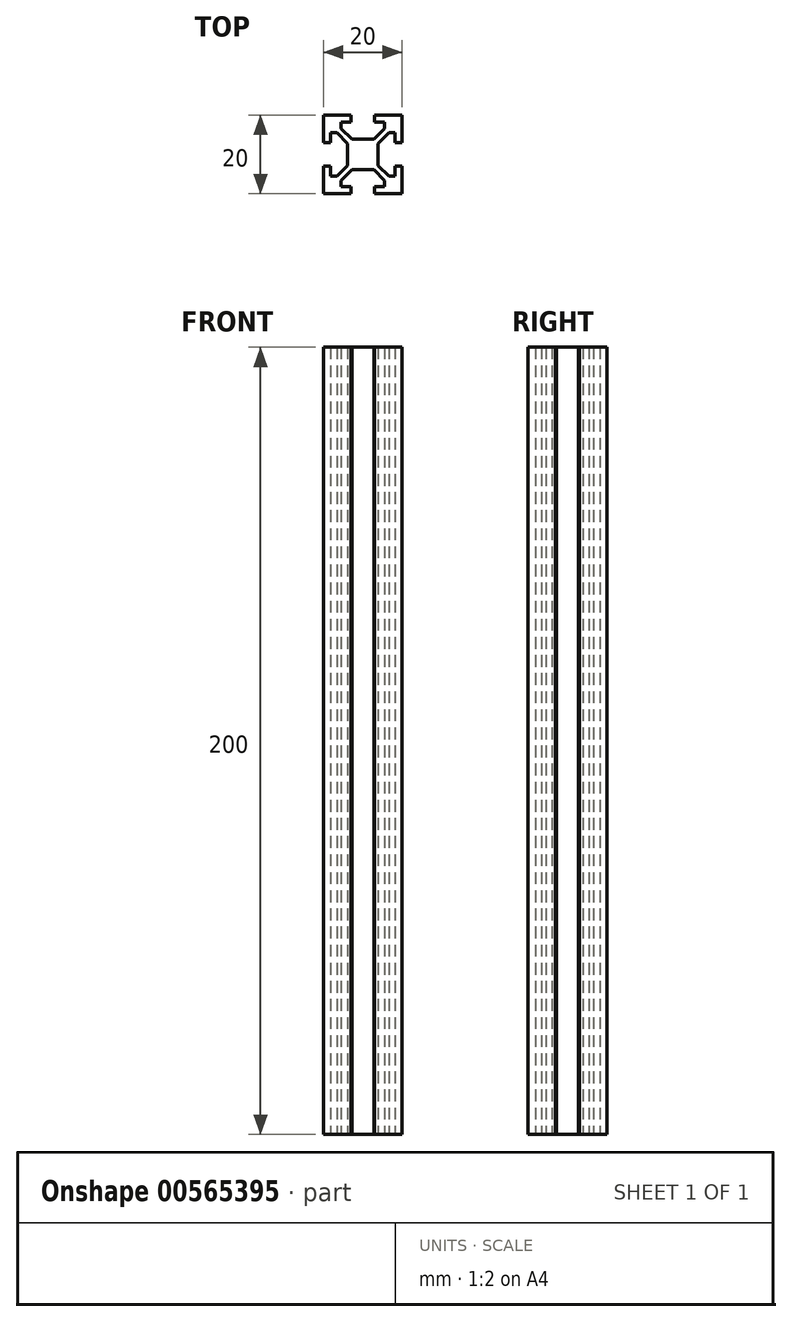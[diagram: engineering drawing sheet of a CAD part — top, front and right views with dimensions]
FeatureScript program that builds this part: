
annotation { "Feature Type Name" : "Feature", "Feature Type Description" : "" }
export const myFeature = defineFeature(function(context is Context, id is Id, definition is map)
    precondition{}
    {
        {
            var Q0;
            Q0=qCreatedBy(makeId("Top.planeOp"),FACE);
            var sketch = newSketch(context, id + "F0", { "sketchPlane" : qUnion([Q0])});
            skLineSegment(sketch, "E0", {"start": v(-12.7, 17.63) * mm, "end": v(-5.7, 17.63) * mm});
            skLineSegment(sketch, "E1", {"start": v(-5.7, 17.63) * mm, "end": v(-5.7, 15.83) * mm});
            skLineSegment(sketch, "E2", {"start": v(0.3, 15.83) * mm, "end": v(0.3, 17.63) * mm});
            skLineSegment(sketch, "E3", {"start": v(0.3, 17.63) * mm, "end": v(7.3, 17.63) * mm});
            skLineSegment(sketch, "E4", {"start": v(-12.7, 17.63) * mm, "end": v(-12.7, 10.63) * mm});
            skLineSegment(sketch, "E5", {"start": v(-12.7, 10.63) * mm, "end": v(-10.9, 10.63) * mm});
            skLineSegment(sketch, "E6", {"start": v(-12.7, 4.63) * mm, "end": v(-12.7, -2.37) * mm});
            skLineSegment(sketch, "E7", {"start": v(-12.7, 4.63) * mm, "end": v(-10.9, 4.63) * mm});
            skLineSegment(sketch, "E8", {"start": v(-12.7, -2.37) * mm, "end": v(-5.7, -2.37) * mm});
            skLineSegment(sketch, "E9", {"start": v(-5.7, -2.37) * mm, "end": v(-5.7, -0.57) * mm});
            skLineSegment(sketch, "E10", {"start": v(0.3, -2.37) * mm, "end": v(7.3, -2.37) * mm});
            skLineSegment(sketch, "E11", {"start": v(0.3, -2.37) * mm, "end": v(0.3, -0.57) * mm});
            skLineSegment(sketch, "E12", {"start": v(7.3, 17.63) * mm, "end": v(7.3, 10.63) * mm});
            skLineSegment(sketch, "E13", {"start": v(7.3, 10.63) * mm, "end": v(5.5, 10.63) * mm});
            skLineSegment(sketch, "E14", {"start": v(7.3, -2.37) * mm, "end": v(7.3, 4.63) * mm});
            skLineSegment(sketch, "E15", {"start": v(7.3, 4.63) * mm, "end": v(5.5, 4.63) * mm});
            skLineSegment(sketch, "E16", {"start": v(-5.7, -0.57) * mm, "end": v(-8.2, -0.57) * mm});
            skLineSegment(sketch, "E17", {"start": v(0.3, -0.57) * mm, "end": v(2.8, -0.57) * mm});
            skLineSegment(sketch, "E18", {"start": v(5.5, 4.63) * mm, "end": v(5.5, 2.13) * mm});
            skLineSegment(sketch, "E19", {"start": v(5.5, 10.63) * mm, "end": v(5.5, 13.13) * mm});
            skLineSegment(sketch, "E20", {"start": v(0.3, 15.83) * mm, "end": v(2.8, 15.83) * mm});
            skLineSegment(sketch, "E21", {"start": v(-5.7, 15.83) * mm, "end": v(-8.2, 15.83) * mm});
            skLineSegment(sketch, "E22", {"start": v(-10.9, 10.63) * mm, "end": v(-10.9, 13.13) * mm});
            skLineSegment(sketch, "E23", {"start": v(-10.9, 4.63) * mm, "end": v(-10.9, 2.13) * mm});
            skLineSegment(sketch, "E24", {"start": v(-10.9, 2.13) * mm, "end": v(-9.3, 2.13) * mm});
            skLineSegment(sketch, "E25", {"start": v(-10.9, 13.13) * mm, "end": v(-9.3, 13.13) * mm});
            skLineSegment(sketch, "E26", {"start": v(-8.2, -0.57) * mm, "end": v(-8.2, 1.03) * mm});
            skLineSegment(sketch, "E27", {"start": v(2.8, -0.57) * mm, "end": v(2.8, 1.03) * mm});
            skLineSegment(sketch, "E28", {"start": v(5.5, 2.13) * mm, "end": v(3.9, 2.13) * mm});
            skLineSegment(sketch, "E29", {"start": v(5.5, 13.13) * mm, "end": v(3.9, 13.13) * mm});
            skLineSegment(sketch, "E30", {"start": v(2.8, 15.83) * mm, "end": v(2.8, 14.23) * mm});
            skLineSegment(sketch, "E31", {"start": v(-8.2, 15.83) * mm, "end": v(-8.2, 14.23) * mm});
            skLineSegment(sketch, "E32", {"start": v(2.8, 14.23) * mm, "end": v(0.1, 11.53) * mm});
            skLineSegment(sketch, "E33", {"start": v(3.9, 13.13) * mm, "end": v(1.2, 10.43) * mm});
            skLineSegment(sketch, "E34", {"start": v(3.9, 2.13) * mm, "end": v(1.2, 4.83) * mm});
            skLineSegment(sketch, "E35", {"start": v(2.8, 1.03) * mm, "end": v(0.1, 3.73) * mm});
            skLineSegment(sketch, "E36", {"start": v(-8.2, 1.03) * mm, "end": v(-5.5, 3.73) * mm});
            skLineSegment(sketch, "E37", {"start": v(-9.3, 2.13) * mm, "end": v(-6.6, 4.83) * mm});
            skLineSegment(sketch, "E38", {"start": v(-9.3, 13.13) * mm, "end": v(-6.6, 10.43) * mm});
            skLineSegment(sketch, "E39", {"start": v(-8.2, 14.23) * mm, "end": v(-5.5, 11.53) * mm});
            skLineSegment(sketch, "E40", {"start": v(-5.5, 11.53) * mm, "end": v(0.1, 11.53) * mm});
            skLineSegment(sketch, "E41", {"start": v(1.2, 10.43) * mm, "end": v(1.2, 4.83) * mm});
            skLineSegment(sketch, "E42", {"start": v(0.1, 3.73) * mm, "end": v(-5.5, 3.73) * mm});
            skLineSegment(sketch, "E43", {"start": v(-6.6, 4.83) * mm, "end": v(-6.6, 10.43) * mm});
            skSolve(sketch);
        }
        {
            var Q0;
            Q0=makeQuery(id+"F0.imprint","IMPRINT",FACE,{"disambiguationData":[TD([[makeQuery(id+"F0.imprint","IMPRINT",EDGE,{"derivedFrom":sQuery(id+"F0.wireOp",EDGE,"E0")}),-1.0]])]});
            extrude(context, id + "F1", {"entities" : qUnion([Q0]), "depth" : 200 * mm, "offsetDistance" : 25 * mm});
        }
    });
